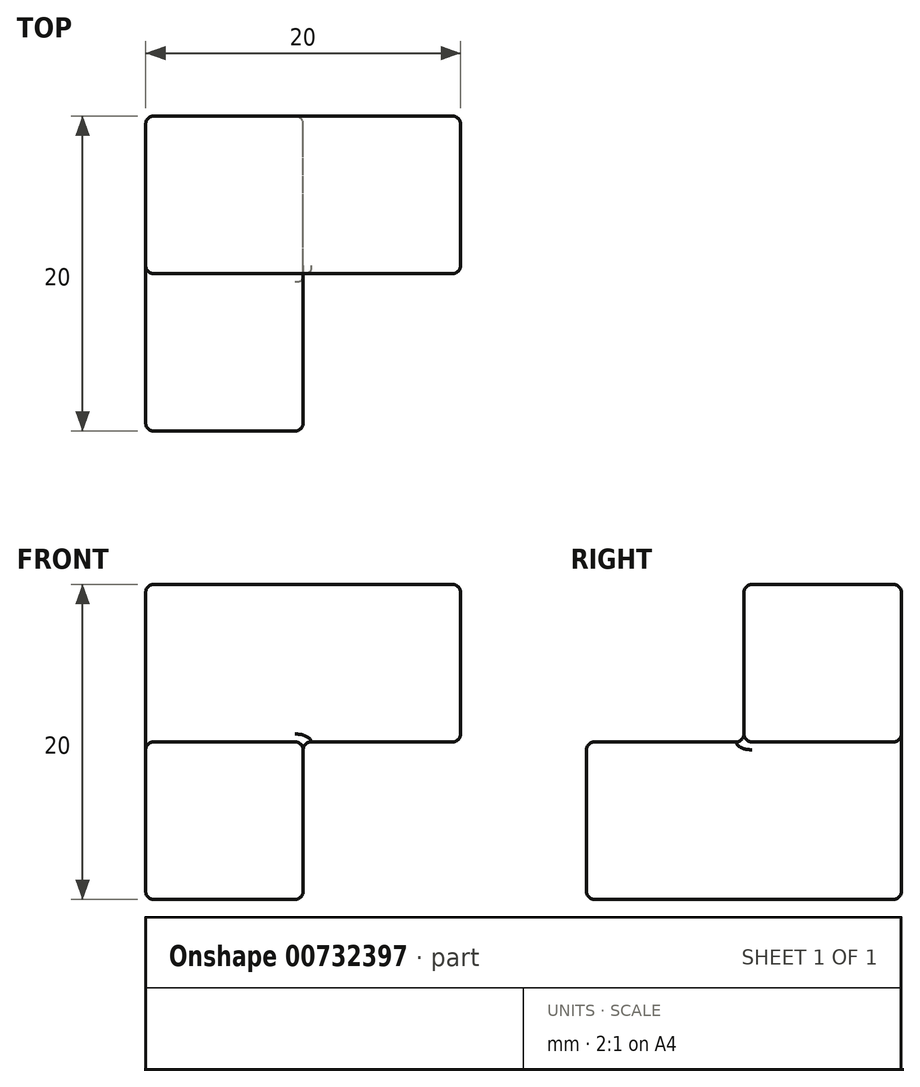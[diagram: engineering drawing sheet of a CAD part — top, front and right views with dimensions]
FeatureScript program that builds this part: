
annotation { "Feature Type Name" : "Feature", "Feature Type Description" : "" }
export const myFeature = defineFeature(function(context is Context, id is Id, definition is map)
    precondition{}
    {
        {
            var Q0;
            Q0=qCreatedBy(makeId("Front.planeOp"),FACE);
            var sketch = newSketch(context, id + "F0", { "sketchPlane" : qUnion([Q0])});
            skLineSegment(sketch, "E0.bottom", {"start": v(5, 10) * mm, "end": v(-5, 10) * mm});
            skLineSegment(sketch, "E0.top", {"start": v(5, -10) * mm, "end": v(-5, -10) * mm});
            skLineSegment(sketch, "E0.left", {"start": v(5, 10) * mm, "end": v(5, -10) * mm});
            skLineSegment(sketch, "E0.right", {"start": v(-5, 10) * mm, "end": v(-5, -10) * mm});
            skPoint(sketch, "E0.middle", {"position": v(0, 0) * mm});
            skLineSegment(sketch, "E1", {"start": v(5, 10) * mm, "end": v(15, 10) * mm});
            skLineSegment(sketch, "E2", {"start": v(15, 10) * mm, "end": v(15, 0) * mm});
            skLineSegment(sketch, "E3", {"start": v(15, 0) * mm, "end": v(5, 0) * mm});
            skLineSegment(sketch, "E4", {"start": v(5, 0) * mm, "end": v(-5, 0) * mm});
            skSolve(sketch);
        }
        {
            var Q0;
            {var subQ0=sQuery(id+"F0.wireOp",EDGE,"E0.bottom");Q0=makeQuery(id+"F0.imprint","IMPRINT",FACE,{"disambiguationData":[TD([[makeQuery(id+"F0.imprint","IMPRINT",EDGE,{"derivedFrom":subQ0}),1.0]])]});}
            var Q1;
            {var subQ0=sQuery(id+"F0.wireOp",EDGE,"E1");Q1=makeQuery(id+"F0.imprint","IMPRINT",FACE,{"disambiguationData":[TD([[makeQuery(id+"F0.imprint","IMPRINT",EDGE,{"derivedFrom":subQ0}),-1.0]])]});}
            extrude(context, id + "F1", {"entities" : qUnion([Q0, Q1]), "depth" : 10 * mm, "offsetDistance" : 25 * mm});
        }
        {
            var Q0;
            {var subQ0=sQuery(id+"F0.wireOp",EDGE,"E0.top");Q0=makeQuery(id+"F0.imprint","IMPRINT",FACE,{"disambiguationData":[TD([[makeQuery(id+"F0.imprint","IMPRINT",EDGE,{"derivedFrom":subQ0}),-1.0]])]});}
            extrude(context, id + "F2", {"entities" : qUnion([Q0]), "operationType" : NewBodyOperationType.ADD, "depth" : 20 * mm, "offsetDistance" : 25 * mm});
        }
        {
            var Q0;
            {var subQ0=sQuery(id+"F0.wireOp",EDGE,"E4");var subQ1=sQuery(id+"F0.wireOp",EDGE,"E0.right");Q0=makeQuery(id+"F2.boolean.opBoolean","MERGE",FACE,{"derivedFrom":[makeQuery(id+"F1.opExtrude","CAP_FACE",FACE,{"disambiguationData":[OSD([sQuery(id+"F0.wireOp",EDGE,"E0.bottom"),subQ1,sQuery(id+"F0.wireOp",EDGE,"E1"),sQuery(id+"F0.wireOp",EDGE,"E2"),sQuery(id+"F0.wireOp",EDGE,"E3"),subQ0])],"isStart":true}),makeQuery(id+"F2.opExtrude","CAP_FACE",FACE,{"disambiguationData":[OSD([sQuery(id+"F0.wireOp",EDGE,"E0.top"),sQuery(id+"F0.wireOp",EDGE,"E0.left"),subQ1,subQ0])],"isStart":true})]});}
            var Q1;
            {var subQ0=sQuery(id+"F0.wireOp",EDGE,"E0.right");Q1=makeQuery(id+"F2.boolean.opBoolean","MERGE",FACE,{"derivedFrom":[makeQuery(id+"F1.opExtrude","SWEPT_FACE",FACE,{"disambiguationData":[OSD([subQ0])]}),makeQuery(id+"F2.opExtrude","SWEPT_FACE",FACE,{"disambiguationData":[OSD([subQ0])]})]});}
            var Q2;
            Q2=makeQuery(id+"F2.opExtrude","SWEPT_FACE",FACE,{"disambiguationData":[OSD([sQuery(id+"F0.wireOp",EDGE,"E0.top")])]});
            var Q3;
            Q3=makeQuery(id+"F2.opExtrude","SWEPT_FACE",FACE,{"disambiguationData":[OSD([sQuery(id+"F0.wireOp",EDGE,"E0.left")])]});
            var Q4;
            Q4=makeQuery(id+"F1.opExtrude","SWEPT_FACE",FACE,{"disambiguationData":[OSD([sQuery(id+"F0.wireOp",EDGE,"E2")])]});
            var Q5;
            Q5=makeQuery(id+"F1.opExtrude","CAP_FACE",FACE,{"disambiguationData":[OSD([sQuery(id+"F0.wireOp",EDGE,"E0.bottom"),sQuery(id+"F0.wireOp",EDGE,"E0.right"),sQuery(id+"F0.wireOp",EDGE,"E1"),sQuery(id+"F0.wireOp",EDGE,"E2"),sQuery(id+"F0.wireOp",EDGE,"E3"),sQuery(id+"F0.wireOp",EDGE,"E4")])],"isStart":false});
            var Q6;
            Q6=makeQuery(id+"F2.opExtrude","CAP_FACE",FACE,{"disambiguationData":[OSD([sQuery(id+"F0.wireOp",EDGE,"E0.top"),sQuery(id+"F0.wireOp",EDGE,"E0.left"),sQuery(id+"F0.wireOp",EDGE,"E0.right"),sQuery(id+"F0.wireOp",EDGE,"E4")])],"isStart":false});
            fillet(context, id + "F3", {"entities" : qUnion([Q0, Q1, Q2, Q3, Q4, Q5, Q6]), "radius" : 0.5 * mm, "tangentPropagation" : true, "allowEdgeOverflow" : false});
        }
    });
